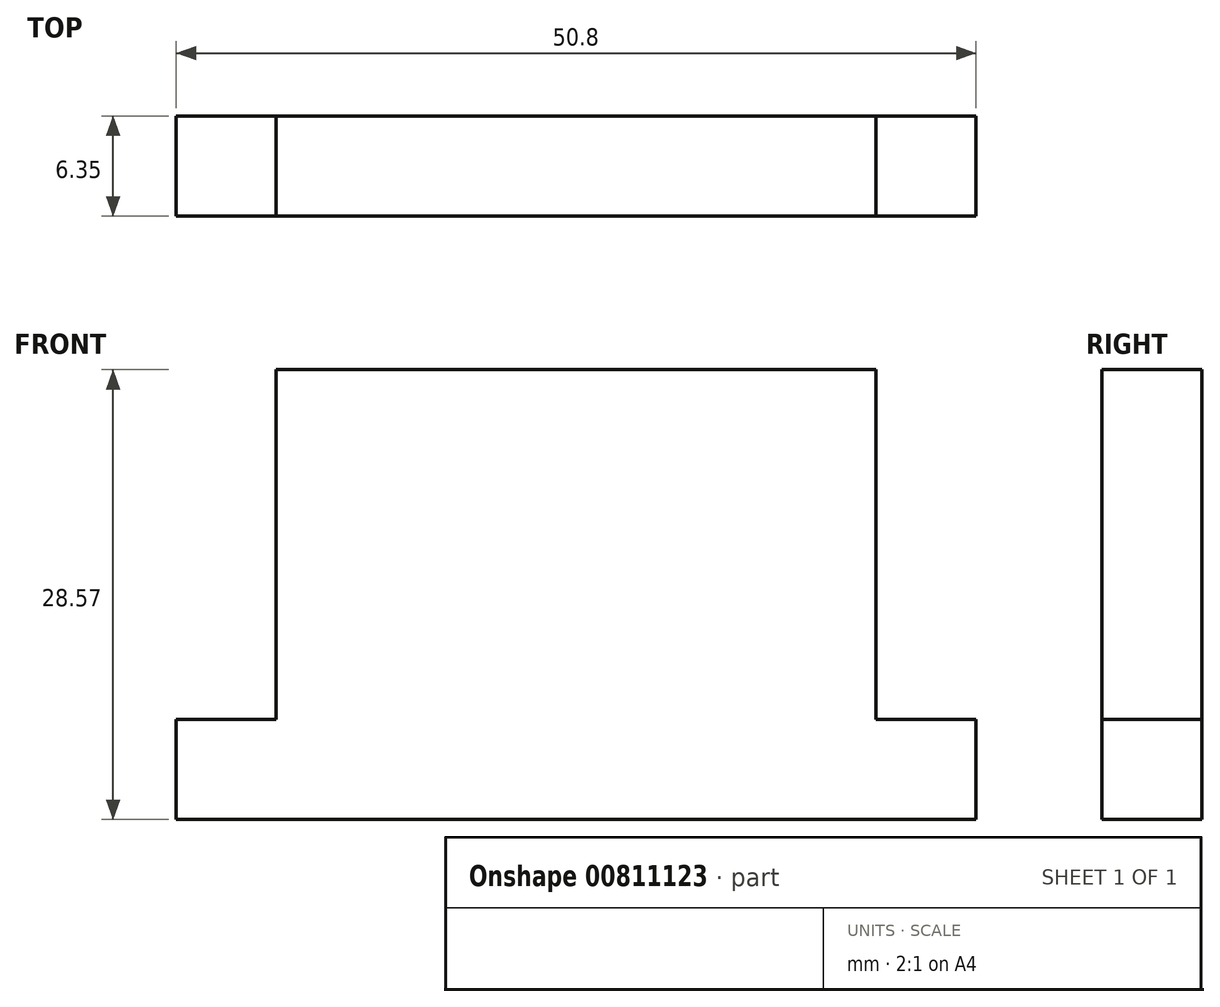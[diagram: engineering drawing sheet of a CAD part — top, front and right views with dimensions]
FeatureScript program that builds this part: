
annotation { "Feature Type Name" : "Feature", "Feature Type Description" : "" }
export const myFeature = defineFeature(function(context is Context, id is Id, definition is map)
    precondition{}
    {
        {
            var Q0;
            Q0=qCreatedBy(makeId("Front.planeOp"),FACE);
            var sketch = newSketch(context, id + "F0", { "sketchPlane" : qUnion([Q0])});
            skLineSegment(sketch, "E0", {"start": v(0, 0) * mm, "end": v(0, 6.35) * mm});
            skLineSegment(sketch, "E1", {"start": v(0, 6.35) * mm, "end": v(6.35, 6.35) * mm});
            skLineSegment(sketch, "E2", {"start": v(6.35, 6.35) * mm, "end": v(6.35, 28.57) * mm});
            skLineSegment(sketch, "E3", {"start": v(6.35, 28.57) * mm, "end": v(44.45, 28.57) * mm});
            skLineSegment(sketch, "E4", {"start": v(44.45, 28.57) * mm, "end": v(44.45, 6.35) * mm});
            skLineSegment(sketch, "E5", {"start": v(44.45, 6.35) * mm, "end": v(50.8, 6.35) * mm});
            skLineSegment(sketch, "E6", {"start": v(50.8, 6.35) * mm, "end": v(50.8, 0) * mm});
            skLineSegment(sketch, "E7", {"start": v(50.8, 0) * mm, "end": v(0, 0) * mm});
            skSolve(sketch);
        }
        {
            var Q0;
            Q0 = qSketchRegion(id + "F0", true);
            extrude(context, id + "F1", {"entities" : qUnion([Q0]), "oppositeDirection" : true, "depth" : 6.35 * mm, "offsetDistance" : 25.4 * mm});
        }
    });
